# Revit family: lb-150_200df8-50_50Hz
name_source: partatom
category: 機械設備
units: mm (PartAtom-declared; Revit-internal decimal feet)

## family parameters
OmniClass タイトル = Heat Exchangers for Ventilation Air
OmniClass 番号 = 23.75.10.34.21
パーツ タイプ = 標準
ロード時にボイドで切り取り = いいえ
丸型コネクタ寸法 = 直径を使用
作業面ベース = いいえ
共有 = いいえ
常に垂直 = はい
部屋計算ポイント = いいえ

## types (2) — shared parameters
Clearance Right = 600
Depth = 1730  [stored 5.67585 ft]
Duct_EA_D = 98  [stored 0.321522 ft]
Duct_EA_W = 61  [stored 0.200131 ft]
Duct_Height = 80  [stored 0.262467 ft]
Duct_OA_D = 458
Duct_RA_H = 372  [stored 1.22047 ft]
Duct_SA_W = 165
EAサイズ_D = 352  [stored 1.15486 ft]
Height = 2047  [stored 6.71588 ft]
IfcExportAs = IfcAirToAirHeatRecoveryType
IfcExportType = ROTARYWHEEL
MAX静圧 = 185.0 Pa
MID静圧 = 0.0 Pa
MID風量 = 0.0 m³/h
MIN静圧 = 0.0 Pa
MIN風量 = 0.0 m³/h
OAサイズ_D = 352  [stored 1.15486 ft]
OmniClassCode = 23-27 23 19 11
RAサイズ_D = 352  [stored 1.15486 ft]
SAサイズ_W = 352  [stored 1.15486 ft]
URL = https://www.mitsubishielectric.co.jp
Uniclass2015Code = Pr_60_60_36_88
Uniclass2015Title = Thermal wheels
Uniclass2015Version = Systems v1.9
Width = 590  [stored 1.9357 ft]
エンタルピ交換効率_冷房 = 67.00%
ドレン管_Depth = 37  [stored 0.121391 ft]
ドレン管_H = 41
ドレン管_W = 200
ドレン管径 = 34 mm
メンテナンススペース = はい
仕様書バージョン = Version1.0
企業コード = 108420
冷媒ガス管_Depth = 95
冷媒ガス管_H = 55  [stored 0.180446 ft]
冷媒ガス管_W = 52
冷媒ガス管径 = 16 mm
冷媒液管_Depth = 59
冷媒液管_H = 169
冷媒液管_W = 127
冷媒液管径 = 10 mm
分類コード = 50052504100050
初期抵抗 = 0.0 Pa
加湿給水管径 = 22 mm
参照している仕様書等のバージョン = 公共建築工事標準仕様書（機械設備工事編）平成31年度版
周波数 = 50 Hz
呼称 = 全熱交換ユニット
外気量 = 0.0 m³/h
実風量 = 0.0 m³/h
形式 = 床置形
排気量 = 0.0 m³/h
本体マテリアル = 溶融亜鉛めっき鋼板
本体固定用穴_径 = 20  [stored 0.0656168 ft]
本体固定用穴ピッチ1 = 460  [stored 1.50919 ft]
本体固定用穴ピッチ2 = 1680  [stored 5.51181 ft]
極数 = 3
機外静圧 = 185.0 Pa
機外静圧_排気 = 185.0 Pa
法定耐用年数 = 15
温度交換効率 = 70.00%
相 = 3
積算_科目 = 1 空気調和設備
符号 = HEU
給水管_Depth = 29  [stored 0.0951444 ft]
給水管_H = 452  [stored 1.48294 ft]
給水管_W = 133
製品リリース年月 = 2021/4/1
製品出荷対象 = 国内
製造元 = 三菱電機株式会社
設置方法 = 床置形
設計風量 = 0.0 m³/h
説明 = 設備用ロスナイ 床置ビルトイン形加熱加湿付
負荷分類 = 3_ファン類
運転質量 = 0.00 kg
電動機出力 = 0 W
電圧 = 200 V
zero-valued in all types: Clearance Back, Clearance Bottom, Clearance Front, Clearance Left, Clearance Top, 価格

## per-type parameters (varying)
| type | Duct_OA_W | Duct_RA_W | Duct_SA_H | EAサイズ_W | MAX風量 | OAサイズ_W | RAサイズ_W | SAサイズ_D | エンタルピ交換効率_暖房 | 有効加湿量 | 消費電力 | 製品質量 | 質量 | 面風速 | 風量 | 騒音レベル(dB(A)) |
| LB-150DF8-50 | 174  [stored 0.570866 ft] | 125  [stored 0.410105 ft] | 798  [stored 2.61811 ft] | 352  [stored 1.15486 ft] | 1500.0 m³/h | 352  [stored 1.15486 ft] | 352  [stored 1.15486 ft] | 352  [stored 1.15486 ft] | 69.50% | 8.3 | 1260 W | 380.00 kg | 456.00 kg | 3.4 m/s | 1500.0 m³/h | 45 |
| LB-200DF8-50 | 74  [stored 0.242782 ft] | 74  [stored 0.242782 ft] | 698  [stored 2.29003 ft] | 452  [stored 1.48294 ft] | 2000.0 m³/h | 452  [stored 1.48294 ft] | 452  [stored 1.48294 ft] | 452  [stored 1.48294 ft] | 69.00% | 9.7 | 1700 W | 390.00 kg | 468.00 kg | 3.5 m/s | 2000.0 m³/h | 46 |

note: column(s) folded — value = type name in every type: モデル

note: [stored X ft] marks values corroborated as IEEE doubles in the binary element streams (Revit-internal decimal feet)

## geometry (parser evidence)
native form markers: Blend x2
no freeform markers — native parametric forms only
